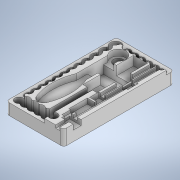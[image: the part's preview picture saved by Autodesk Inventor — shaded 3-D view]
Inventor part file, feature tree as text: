
AUTODESK INVENTOR PART (.ipt)
format: ipt  version: 2020 (Build 240168000, 168)  size: 595,968 bytes
history: native  units: mm
features: extrude x12, sketch x12, fillet x11
ambient origin geometry x8: Origin, YZ Plane, XZ Plane, XY Plane, X Axis, Y Axis, Z Axis, Center Point
bodies: Solide1 (feature_tree)
feature tree (35):
  extrude  "Extrusion1"  Depth=100.0mm
  fillet  "Congé1"  Radius=191.0mm
  extrude  "Extrusion2"  Depth=26.5mm TaperAngle=0.0deg
  extrude  "Extrusion3"  Depth=5.0mm
  fillet  "Congé2"  Radius=15.5mm
  fillet  "Congé3"  Radius=13.0mm
  extrude  "Extrusion4"  Depth=13.0mm
  fillet  "Congé4"  Radius=66.5mm
  fillet  "Congé5"  Radius=7.0mm
  fillet  "Congé6"  Radius=30.0mm
  extrude  "Extrusion5"  Depth=14.0mm
  fillet  "Congé7"  Radius=12.0mm
  fillet  "Congé8"  Radius=13.0mm
  fillet  "Congé9"  Radius=12.0mm
  extrude  "Extrusion6"  Depth=12.0mm
  extrude  "Extrusion7"  Depth=12.0mm
  sketch  "Esquisse9"
  extrude  "Extrusion8"  Depth=12.0mm
  extrude  "Extrusion9"  Depth=10.0mm
  extrude  "Extrusion10"  Depth=13.5mm
  extrude  "Extrusion11"  Depth=7.0mm
  extrude  "Extrusion12"  Depth=7.0mm
  fillet  "Congé12"  Radius=7.0mm
  fillet  "Congé13"  Radius=7.0mm
  sketch  "Esquisse1"
  sketch  "Esquisse2"
  sketch  "Esquisse4"
  sketch  "Esquisse5"
  sketch  "Esquisse6"
  sketch  "Esquisse7"
  sketch  "Esquisse8"
  sketch  "Esquisse10"
  sketch  "Esquisse11"
  sketch  "Esquisse12"
  sketch  "Esquisse13"
